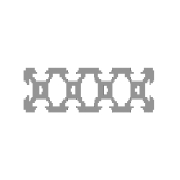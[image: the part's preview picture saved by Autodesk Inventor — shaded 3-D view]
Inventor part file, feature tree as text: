
AUTODESK INVENTOR PART (.ipt)
format: ipt  version: 2013 (Build 170138000, 138)  size: 286,208 bytes
history: native  units: mm
features: other x4, plane x3, split x2, sketch x2
ambient origin geometry x8: Origin, YZ Plane, XZ Plane, XY Plane, X Axis, Y Axis, Z Axis, Center Point
bodies: Solid1 (feature_tree), Body (feature_tree)
feature tree (11):
  other  "Driven Length"
  other  "Frame Generator"
  other  "Start Plane"
  other  "End Plane"
  plane  "Work Plane8"
  split  "Split1"
  plane  "Work Plane9"
  split  "Split2"
  sketch  "Sketch10"  dims[d0=10.0mm]
  plane  "Work Plane7"
  sketch  "Sketch11"  dims[d1=10.0mm d2=10.0mm d3=4.2mm d4=1.5mm d5=45.0deg d6=1.64mm d7=1.8mm d8=10.0mm d9=2.84mm d11=135.0deg d12=1.96mm d13=5.68mm d14=2.0mm d17=-10.0mm d18=485.0mm d19=0.13mm d20=0.0mm d29=90.0deg d22=495.0mm]
